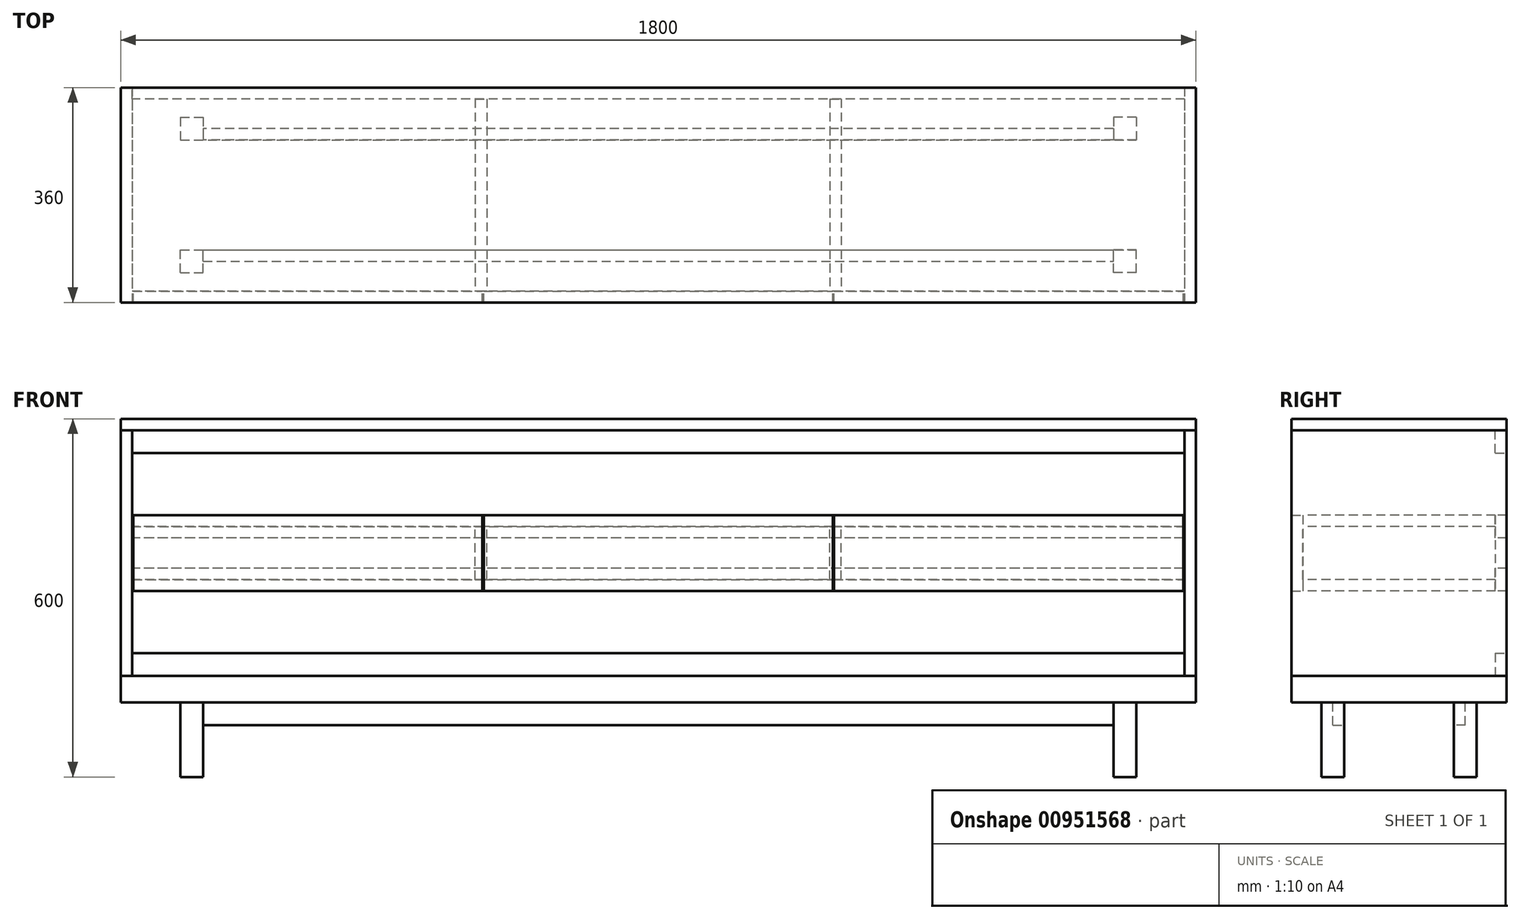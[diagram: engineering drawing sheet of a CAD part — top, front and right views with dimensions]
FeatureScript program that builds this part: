
annotation { "Feature Type Name" : "Feature", "Feature Type Description" : "" }
export const myFeature = defineFeature(function(context is Context, id is Id, definition is map)
    precondition{}
    {
        {
            var Q0;
            Q0=qCreatedBy(makeId("Front.planeOp"),FACE);
            var sketch = newSketch(context, id + "F0", { "sketchPlane" : qUnion([Q0])});
            skLineSegment(sketch, "E0.bottom", {"start": v(-900, 205.95) * mm, "end": v(900, 205.95) * mm});
            skLineSegment(sketch, "E0.top", {"start": v(-900, 225) * mm, "end": v(900, 225) * mm});
            skLineSegment(sketch, "E0.left", {"start": v(-900, 205.95) * mm, "end": v(-900, 225) * mm});
            skLineSegment(sketch, "E0.right", {"start": v(900, 205.95) * mm, "end": v(900, 225) * mm});
            skLineSegment(sketch, "E1", {"start": v(0, 205.95) * mm, "end": v(0, 0) * mm, "construction": true});
            skLineSegment(sketch, "E2", {"start": v(-72.2, 0) * mm, "end": v(104.92, 0) * mm, "construction": true});
            skLineSegment(sketch, "E3.bottom", {"start": v(-900, -225) * mm, "end": v(900, -225) * mm});
            skLineSegment(sketch, "E3.top", {"start": v(-900, -205.95) * mm, "end": v(900, -205.95) * mm});
            skLineSegment(sketch, "E3.left", {"start": v(-900, -225) * mm, "end": v(-900, -205.95) * mm});
            skLineSegment(sketch, "E3.right", {"start": v(900, -225) * mm, "end": v(900, -205.95) * mm});
            skLineSegment(sketch, "E4", {"start": v(0, 0) * mm, "end": v(0, -205.95) * mm, "construction": true});
            skSolve(sketch);
        }
        {
            var Q0;
            Q0 = qSketchRegion(id + "F0", true);
            extrude(context, id + "F1", {"entities" : qUnion([Q0]), "depth" : 360 * mm, "offsetDistance" : 25 * mm, "symmetric" : true});
        }
        {
            var Q0;
            Q0=makeQuery(id+"F1.opExtrude","CAP_FACE",FACE,{"disambiguationData":[OSD([sQuery(id+"F0.wireOp",EDGE,"E0.bottom"),sQuery(id+"F0.wireOp",EDGE,"E0.top"),sQuery(id+"F0.wireOp",EDGE,"E0.left"),sQuery(id+"F0.wireOp",EDGE,"E0.right")])],"isStart":false});
            var sketch = newSketch(context, id + "F2", { "sketchPlane" : qUnion([Q0])});
            skLineSegment(sketch, "E5.bottom", {"start": v(-900, 205.95) * mm, "end": v(-880.95, 205.95) * mm});
            skLineSegment(sketch, "E5.top", {"start": v(-900, -205.95) * mm, "end": v(-880.95, -205.95) * mm});
            skLineSegment(sketch, "E5.left", {"start": v(-900, 205.95) * mm, "end": v(-900, -205.95) * mm});
            skLineSegment(sketch, "E5.right", {"start": v(-880.95, 205.95) * mm, "end": v(-880.95, -205.95) * mm});
            skLineSegment(sketch, "E6.bottom", {"start": v(900, 205.95) * mm, "end": v(880.95, 205.95) * mm});
            skLineSegment(sketch, "E6.top", {"start": v(900, -205.95) * mm, "end": v(880.95, -205.95) * mm});
            skLineSegment(sketch, "E6.left", {"start": v(900, 205.95) * mm, "end": v(900, -205.95) * mm});
            skLineSegment(sketch, "E6.right", {"start": v(880.95, 205.95) * mm, "end": v(880.95, -205.95) * mm});
            skSolve(sketch);
        }
        {
            var Q0;
            Q0 = qSketchRegion(id + "F2", true);
            var Q1;
            Q1=makeQuery(id+"F1.opExtrude","CAP_FACE",FACE,{"disambiguationData":[OSD([sQuery(id+"F0.wireOp",EDGE,"E0.bottom"),sQuery(id+"F0.wireOp",EDGE,"E0.top"),sQuery(id+"F0.wireOp",EDGE,"E0.left"),sQuery(id+"F0.wireOp",EDGE,"E0.right")])],"isStart":true});
            extrude(context, id + "F3", {"entities" : qUnion([Q0]), "endBound" : BoundingType.UP_TO_SURFACE, "oppositeDirection" : true, "depth" : 25 * mm, "endBoundEntityFace" : qUnion([Q1]), "offsetDistance" : 25 * mm});
        }
        {
            var Q0;
            Q0=makeQuery(id+"F1.opExtrude","CAP_FACE",FACE,{"disambiguationData":[OSD([sQuery(id+"F0.wireOp",EDGE,"E0.bottom"),sQuery(id+"F0.wireOp",EDGE,"E0.top"),sQuery(id+"F0.wireOp",EDGE,"E0.left"),sQuery(id+"F0.wireOp",EDGE,"E0.right")])],"isStart":false});
            var sketch = newSketch(context, id + "F4", { "sketchPlane" : qUnion([Q0])});
            skLineSegment(sketch, "E7.bottom", {"start": v(-880.95, 63.5) * mm, "end": v(880.95, 63.5) * mm});
            skLineSegment(sketch, "E7.top", {"start": v(-880.95, 44.45) * mm, "end": v(880.95, 44.45) * mm});
            skLineSegment(sketch, "E7.left", {"start": v(-880.95, 63.5) * mm, "end": v(-880.95, 44.45) * mm});
            skLineSegment(sketch, "E7.right", {"start": v(880.95, 63.5) * mm, "end": v(880.95, 44.45) * mm});
            skLineSegment(sketch, "E8.bottom", {"start": v(880.95, -44.45) * mm, "end": v(-880.95, -44.45) * mm});
            skLineSegment(sketch, "E8.top", {"start": v(880.95, -63.5) * mm, "end": v(-880.95, -63.5) * mm});
            skLineSegment(sketch, "E8.left", {"start": v(880.95, -44.45) * mm, "end": v(880.95, -63.5) * mm});
            skLineSegment(sketch, "E8.right", {"start": v(-880.95, -44.45) * mm, "end": v(-880.95, -63.5) * mm});
            skLineSegment(sketch, "E9", {"start": v(0, 63.5) * mm, "end": v(0, 205.95) * mm, "construction": true});
            skLineSegment(sketch, "E10", {"start": v(0, -63.5) * mm, "end": v(0, -205.95) * mm, "construction": true});
            skSolve(sketch);
        }
        {
            var Q0;
            Q0 = qSketchRegion(id + "F4", true);
            var Q1;
            Q1=makeQuery(id+"F1.opExtrude","CAP_FACE",FACE,{"disambiguationData":[OSD([sQuery(id+"F0.wireOp",EDGE,"E3.bottom"),sQuery(id+"F0.wireOp",EDGE,"E3.top"),sQuery(id+"F0.wireOp",EDGE,"E3.left"),sQuery(id+"F0.wireOp",EDGE,"E3.right")])],"isStart":true});
            extrude(context, id + "F5", {"entities" : qUnion([Q0]), "oppositeDirection" : true, "depth" : (360 - 19.05) * mm, "endBoundEntityFace" : qUnion([Q1]), "offsetDistance" : 25 * mm});
        }
        {
            var Q0;
            Q0=makeQuery(id+"F3.opExtrude","SWEPT_FACE",FACE,{"disambiguationData":[OSD([sQuery(id+"F2.wireOp",EDGE,"E5.right")])]});
            var sketch = newSketch(context, id + "F6", { "sketchPlane" : qUnion([Q0])});
            skLineSegment(sketch, "E11.bottom", {"start": v(160.95, 63.5) * mm, "end": v(180, 63.5) * mm});
            skLineSegment(sketch, "E11.top", {"start": v(160.95, 25.4) * mm, "end": v(180, 25.4) * mm});
            skLineSegment(sketch, "E11.left", {"start": v(160.95, 63.5) * mm, "end": v(160.95, 25.4) * mm});
            skLineSegment(sketch, "E11.right", {"start": v(180, 63.5) * mm, "end": v(180, 25.4) * mm});
            skLineSegment(sketch, "E12.bottom", {"start": v(160.95, -25.4) * mm, "end": v(180, -25.4) * mm});
            skLineSegment(sketch, "E12.top", {"start": v(160.95, -63.5) * mm, "end": v(180, -63.5) * mm});
            skLineSegment(sketch, "E12.left", {"start": v(160.95, -25.4) * mm, "end": v(160.95, -63.5) * mm});
            skLineSegment(sketch, "E12.right", {"start": v(180, -25.4) * mm, "end": v(180, -63.5) * mm});
            skLineSegment(sketch, "E13.bottom", {"start": v(180, 205.95) * mm, "end": v(160.95, 205.95) * mm});
            skLineSegment(sketch, "E13.top", {"start": v(180, 167.85) * mm, "end": v(160.95, 167.85) * mm});
            skLineSegment(sketch, "E13.left", {"start": v(180, 205.95) * mm, "end": v(180, 167.85) * mm});
            skLineSegment(sketch, "E13.right", {"start": v(160.95, 205.95) * mm, "end": v(160.95, 167.85) * mm});
            skLineSegment(sketch, "E14.bottom", {"start": v(180, -205.95) * mm, "end": v(160.95, -205.95) * mm});
            skLineSegment(sketch, "E14.top", {"start": v(180, -167.85) * mm, "end": v(160.95, -167.85) * mm});
            skLineSegment(sketch, "E14.left", {"start": v(180, -205.95) * mm, "end": v(180, -167.85) * mm});
            skLineSegment(sketch, "E14.right", {"start": v(160.95, -205.95) * mm, "end": v(160.95, -167.85) * mm});
            skSolve(sketch);
        }
        {
            var Q0;
            Q0 = qSketchRegion(id + "F6", true);
            var Q1;
            Q1=makeQuery(id+"F3.opExtrude","SWEPT_FACE",FACE,{"disambiguationData":[OSD([sQuery(id+"F2.wireOp",EDGE,"E6.right")])]});
            extrude(context, id + "F7", {"entities" : qUnion([Q0]), "endBound" : BoundingType.UP_TO_SURFACE, "depth" : 25 * mm, "endBoundEntityFace" : qUnion([Q1]), "offsetDistance" : 25 * mm});
        }
        {
            var Q0;
            Q0=makeQuery(id+"F5.opExtrude","CAP_FACE",FACE,{"disambiguationData":[OSD([sQuery(id+"F4.wireOp",EDGE,"E7.bottom"),sQuery(id+"F4.wireOp",EDGE,"E7.top"),sQuery(id+"F4.wireOp",EDGE,"E7.left"),sQuery(id+"F4.wireOp",EDGE,"E7.right")])],"isStart":true});
            var sketch = newSketch(context, id + "F8", { "sketchPlane" : qUnion([Q0])});
            skLineSegment(sketch, "E15.bottom", {"start": v(-306.35, 44.45) * mm, "end": v(-287.3, 44.45) * mm});
            skLineSegment(sketch, "E15.top", {"start": v(-306.35, -44.45) * mm, "end": v(-287.3, -44.45) * mm});
            skLineSegment(sketch, "E15.left", {"start": v(-306.35, 44.45) * mm, "end": v(-306.35, -44.45) * mm});
            skLineSegment(sketch, "E15.right", {"start": v(-287.3, 44.45) * mm, "end": v(-287.3, -44.45) * mm});
            skLineSegment(sketch, "E16.bottom", {"start": v(287.3, 44.45) * mm, "end": v(306.35, 44.45) * mm});
            skLineSegment(sketch, "E16.top", {"start": v(287.3, -44.45) * mm, "end": v(306.35, -44.45) * mm});
            skLineSegment(sketch, "E16.left", {"start": v(287.3, 44.45) * mm, "end": v(287.3, -44.45) * mm});
            skLineSegment(sketch, "E16.right", {"start": v(306.35, 44.45) * mm, "end": v(306.35, -44.45) * mm});
            skLineSegment(sketch, "E17", {"start": v(-306.35, 0) * mm, "end": v(-880.95, 0) * mm, "construction": true});
            skLineSegment(sketch, "E18", {"start": v(-287.3, 0) * mm, "end": v(287.3, 0) * mm, "construction": true});
            skLineSegment(sketch, "E19", {"start": v(306.35, 0) * mm, "end": v(880.95, 0) * mm, "construction": true});
            skSolve(sketch);
        }
        {
            var Q0;
            Q0 = qSketchRegion(id + "F8", true);
            var Q1;
            Q1=makeQuery(id+"F7.opExtrude","SWEPT_FACE",FACE,{"disambiguationData":[OSD([sQuery(id+"F6.wireOp",EDGE,"E11.left")])]});
            extrude(context, id + "F9", {"entities" : qUnion([Q0]), "endBound" : BoundingType.UP_TO_SURFACE, "oppositeDirection" : true, "depth" : 25 * mm, "endBoundEntityFace" : qUnion([Q1]), "offsetDistance" : 25 * mm});
        }
        {
            var Q0;
            Q0=makeQuery(id+"F5.opExtrude","CAP_FACE",FACE,{"disambiguationData":[OSD([sQuery(id+"F4.wireOp",EDGE,"E7.bottom"),sQuery(id+"F4.wireOp",EDGE,"E7.top"),sQuery(id+"F4.wireOp",EDGE,"E7.left"),sQuery(id+"F4.wireOp",EDGE,"E7.right")])],"isStart":true});
            var sketch = newSketch(context, id + "F10", { "sketchPlane" : qUnion([Q0])});
            skLineSegment(sketch, "E20.bottom", {"start": v(-880.95, 63.5) * mm, "end": v(880.95, 63.5) * mm});
            skLineSegment(sketch, "E20.top", {"start": v(-880.95, -63.5) * mm, "end": v(880.95, -63.5) * mm});
            skLineSegment(sketch, "E20.left", {"start": v(-880.95, 63.5) * mm, "end": v(-880.95, -63.5) * mm});
            skLineSegment(sketch, "E20.right", {"start": v(880.95, 63.5) * mm, "end": v(880.95, -63.5) * mm});
            skSolve(sketch);
        }
        {
            var Q0;
            Q0 = qSketchRegion(id + "F10", true);
            extrude(context, id + "F11", {"entities" : qUnion([Q0]), "operationType" : NewBodyOperationType.REMOVE, "oppositeDirection" : true, "depth" : 19.05 * mm, "offsetDistance" : 25 * mm});
        }
        {
            var Q0;
            Q0=makeQuery(id+"F11.boolean.opBoolean","COPY",FACE,{"disambiguationData":[TD([makeQuery(id+"F5.opExtrude","SWEPT_FACE",FACE,{"disambiguationData":[OSD([sQuery(id+"F4.wireOp",EDGE,"E7.bottom")])]})])],"derivedFrom":makeQuery(id+"F11.opExtrude","CAP_FACE",FACE,{"disambiguationData":[OSD([sQuery(id+"F10.wireOp",EDGE,"E20.bottom"),sQuery(id+"F10.wireOp",EDGE,"E20.top"),sQuery(id+"F10.wireOp",EDGE,"E20.left"),sQuery(id+"F10.wireOp",EDGE,"E20.right")])],"isStart":false})});
            var sketch = newSketch(context, id + "F12", { "sketchPlane" : qUnion([Q0])});
            skLineSegment(sketch, "E21.bottom", {"start": v(-878.95, 63.5) * mm, "end": v(-294.32, 63.5) * mm});
            skLineSegment(sketch, "E21.top", {"start": v(-878.95, -63.5) * mm, "end": v(-294.32, -63.5) * mm});
            skLineSegment(sketch, "E21.left", {"start": v(-878.95, 63.5) * mm, "end": v(-878.95, -63.5) * mm});
            skLineSegment(sketch, "E21.right", {"start": v(-294.32, 63.5) * mm, "end": v(-294.32, -63.5) * mm});
            skLineSegment(sketch, "E22.bottom", {"start": v(-292.32, -63.5) * mm, "end": v(292.32, -63.5) * mm});
            skLineSegment(sketch, "E22.top", {"start": v(-292.32, 63.5) * mm, "end": v(292.32, 63.5) * mm});
            skLineSegment(sketch, "E22.left", {"start": v(-292.32, -63.5) * mm, "end": v(-292.32, 63.5) * mm});
            skLineSegment(sketch, "E22.right", {"start": v(292.32, -63.5) * mm, "end": v(292.32, 63.5) * mm});
            skLineSegment(sketch, "E23.bottom", {"start": v(294.32, 63.5) * mm, "end": v(878.95, 63.5) * mm});
            skLineSegment(sketch, "E23.top", {"start": v(294.32, -63.5) * mm, "end": v(878.95, -63.5) * mm});
            skLineSegment(sketch, "E23.left", {"start": v(294.32, 63.5) * mm, "end": v(294.32, -63.5) * mm});
            skLineSegment(sketch, "E23.right", {"start": v(878.95, 63.5) * mm, "end": v(878.95, -63.5) * mm});
            skSolve(sketch);
        }
        {
            var Q0;
            Q0 = qSketchRegion(id + "F12", true);
            extrude(context, id + "F13", {"entities" : qUnion([Q0]), "depth" : 19.05 * mm, "offsetDistance" : 25 * mm});
        }
        {
            var Q0;
            Q0=makeQuery(id+"F1.opExtrude","SWEPT_FACE",FACE,{"disambiguationData":[OSD([sQuery(id+"F0.wireOp",EDGE,"E3.bottom")])]});
            extrude(context, id + "F14", {"entities" : qUnion([Q0]), "operationType" : NewBodyOperationType.ADD, "depth" : 25 * mm, "offsetDistance" : 25 * mm});
        }
        {
            var Q0;
            Q0=makeQuery(id+"F14.opExtrude","CAP_FACE",FACE,{"disambiguationData":[OSD([sQuery(id+"F0.wireOp",EDGE,"E3.bottom")])],"isStart":false});
            var sketch = newSketch(context, id + "F15", { "sketchPlane" : qUnion([Q0])});
            skLineSegment(sketch, "E24.bottom", {"start": v(-800, 130) * mm, "end": v(-761.9, 130) * mm});
            skLineSegment(sketch, "E24.top", {"start": v(-800, 91.9) * mm, "end": v(-761.9, 91.9) * mm});
            skLineSegment(sketch, "E24.left", {"start": v(-800, 130) * mm, "end": v(-800, 91.9) * mm});
            skLineSegment(sketch, "E24.right", {"start": v(-761.9, 130) * mm, "end": v(-761.9, 91.9) * mm});
            skLineSegment(sketch, "E25", {"start": v(-108.3, 0) * mm, "end": v(112.68, 0) * mm, "construction": true});
            skLineSegment(sketch, "E26", {"start": v(0, 53.17) * mm, "end": v(0, -31.25) * mm, "construction": true});
            skLineSegment(sketch, "E27.MirrorCS", {"start": v(800, 130) * mm, "end": v(761.9, 130) * mm});
            skLineSegment(sketch, "E28.MirrorCS", {"start": v(761.9, 130) * mm, "end": v(761.9, 91.9) * mm});
            skLineSegment(sketch, "E29.MirrorCS", {"start": v(800, 130) * mm, "end": v(800, 91.9) * mm});
            skLineSegment(sketch, "E30.MirrorCS", {"start": v(800, 91.9) * mm, "end": v(761.9, 91.9) * mm});
            skLineSegment(sketch, "E31.MirrorCS", {"start": v(-800, -130) * mm, "end": v(-800, -91.9) * mm});
            skLineSegment(sketch, "E32.MirrorCS", {"start": v(-761.9, -130) * mm, "end": v(-761.9, -91.9) * mm});
            skLineSegment(sketch, "E33.MirrorCS", {"start": v(-800, -91.9) * mm, "end": v(-761.9, -91.9) * mm});
            skLineSegment(sketch, "E34.MirrorCS", {"start": v(-800, -130) * mm, "end": v(-761.9, -130) * mm});
            skLineSegment(sketch, "E35.MirrorCS", {"start": v(761.9, -130) * mm, "end": v(761.9, -91.9) * mm});
            skLineSegment(sketch, "E36.MirrorCS", {"start": v(800, -130) * mm, "end": v(800, -91.9) * mm});
            skLineSegment(sketch, "E37.MirrorCS", {"start": v(800, -91.9) * mm, "end": v(761.9, -91.9) * mm});
            skLineSegment(sketch, "E38.MirrorCS", {"start": v(800, -130) * mm, "end": v(761.9, -130) * mm});
            skSolve(sketch);
        }
        {
            var Q0;
            Q0 = qSketchRegion(id + "F15", true);
            extrude(context, id + "F16", {"entities" : qUnion([Q0]), "operationType" : NewBodyOperationType.ADD, "depth" : 125 * mm, "offsetDistance" : 25 * mm});
        }
        {
            var Q0;
            Q0=makeQuery(id+"F14.opExtrude","CAP_FACE",FACE,{"disambiguationData":[OSD([sQuery(id+"F0.wireOp",EDGE,"E3.bottom")])],"isStart":false});
            var sketch = newSketch(context, id + "F17", { "sketchPlane" : qUnion([Q0])});
            skLineSegment(sketch, "E39.bottom", {"start": v(-761.9, 91.9) * mm, "end": v(761.9, 91.9) * mm});
            skLineSegment(sketch, "E39.top", {"start": v(-761.9, 110.95) * mm, "end": v(761.9, 110.95) * mm});
            skLineSegment(sketch, "E39.left", {"start": v(-761.9, 91.9) * mm, "end": v(-761.9, 110.95) * mm});
            skLineSegment(sketch, "E39.right", {"start": v(761.9, 91.9) * mm, "end": v(761.9, 110.95) * mm});
            skLineSegment(sketch, "E40.bottom", {"start": v(761.9, -91.9) * mm, "end": v(-761.9, -91.9) * mm});
            skLineSegment(sketch, "E40.top", {"start": v(761.9, -110.95) * mm, "end": v(-761.9, -110.95) * mm});
            skLineSegment(sketch, "E40.left", {"start": v(761.9, -91.9) * mm, "end": v(761.9, -110.95) * mm});
            skLineSegment(sketch, "E40.right", {"start": v(-761.9, -91.9) * mm, "end": v(-761.9, -110.95) * mm});
            skSolve(sketch);
        }
        {
            var Q0;
            Q0 = qSketchRegion(id + "F17", true);
            extrude(context, id + "F18", {"entities" : qUnion([Q0]), "operationType" : NewBodyOperationType.ADD, "depth" : 38.1 * mm, "offsetDistance" : 25 * mm});
        }
    });
